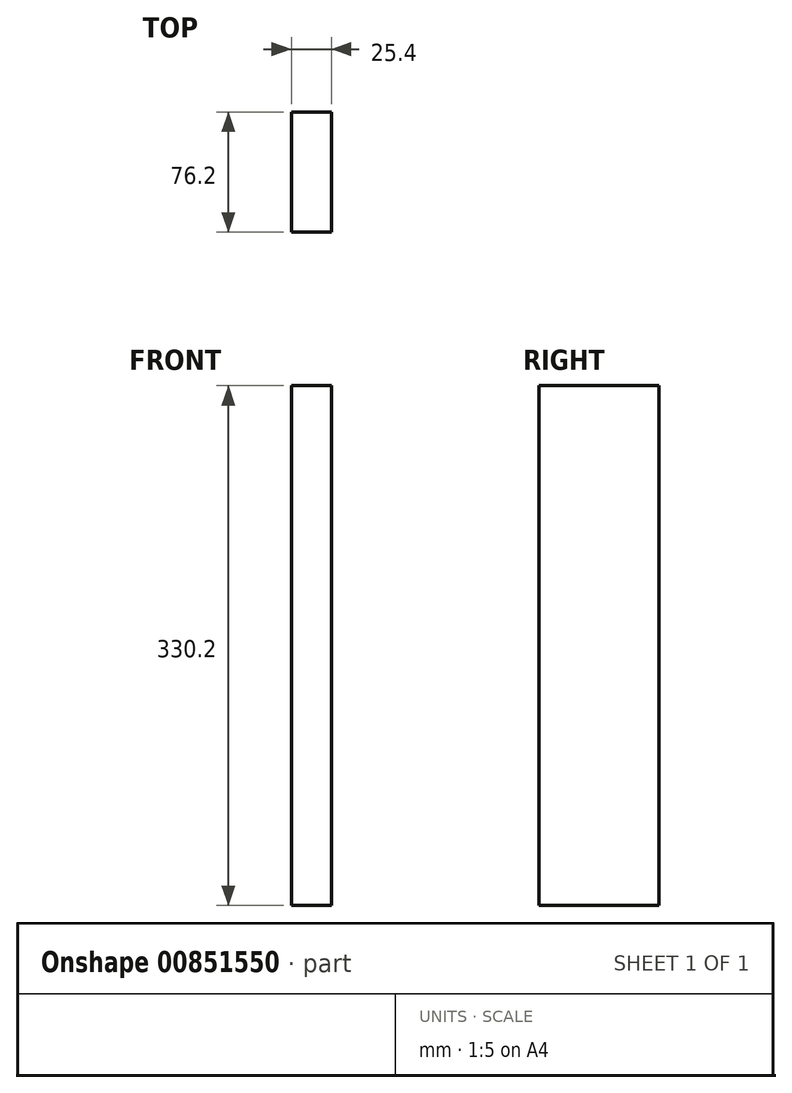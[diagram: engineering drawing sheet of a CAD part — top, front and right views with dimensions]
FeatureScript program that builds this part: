
annotation { "Feature Type Name" : "Feature", "Feature Type Description" : "" }
export const myFeature = defineFeature(function(context is Context, id is Id, definition is map)
    precondition{}
    {
        {
            var Q0;
            Q0=qCreatedBy(makeId("Front.planeOp"),FACE);
            var sketch = newSketch(context, id + "F0", { "sketchPlane" : qUnion([Q0])});
            skLineSegment(sketch, "E0.bottom", {"start": v(-52.38, 167.38) * mm, "end": v(-26.98, 167.38) * mm});
            skLineSegment(sketch, "E0.top", {"start": v(-52.38, -162.82) * mm, "end": v(-26.98, -162.82) * mm});
            skLineSegment(sketch, "E0.left", {"start": v(-52.38, 167.38) * mm, "end": v(-52.38, -162.82) * mm});
            skLineSegment(sketch, "E0.right", {"start": v(-26.98, 167.38) * mm, "end": v(-26.98, -162.82) * mm});
            skSolve(sketch);
        }
        {
            var Q0;
            Q0 = qSketchRegion(id + "F0", true);
            extrude(context, id + "F1", {"entities" : qUnion([Q0]), "depth" : 76.2 * mm, "offsetDistance" : 25.4 * mm});
        }
    });
